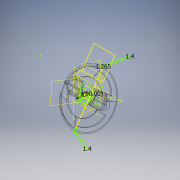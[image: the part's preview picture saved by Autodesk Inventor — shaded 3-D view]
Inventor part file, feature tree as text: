
AUTODESK INVENTOR PART (.ipt)
format: ipt  version: 2018 (Build 220112000, 112)  size: 2,839,552 bytes
history: native  units: mm
features: sketch x125, extrude x112, fillet x31, plane x11, revolve x2, hole x1, direct_edit x1, other x1
ambient origin geometry x8: Origin, YZ Plane, XZ Plane, XY Plane, X Axis, Y Axis, Z Axis, Center Point
bodies: Body1 (feature_tree)
feature tree (284):
  plane  "Work Plane5"
  sketch  "Sketch28"  dims[d118=18.7mm d119=0.0mm d120=0.9mm d121=0.0mm]
  extrude  "Extrusion21"  Depth=0.9mm TaperAngle=0.0deg
  plane  "Work Plane4"
  extrude  "Extrusion22"  Depth=3.8mm
  extrude  "Extrusion23"  Depth=46.7mm
  plane  "Work Plane3"
  hole  "Hole6"  [1 undecoded]
  extrude  "Extrusion27"  Depth=3.8mm
  extrude  "Extrusion28"  Depth=32.03mm
  extrude  "Extrusion30"  Depth=10.0mm TaperAngle=0.0deg
  extrude  "Extrusion31"  Depth=16.3mm TaperAngle=0.0deg
  sketch  "Sketch56"  dims[d188=16.3mm d189=0.0mm d190=16.3mm d191=0.0mm]
  sketch  "Sketch57"  dims[d192=16.3mm d193=0.0mm d194=16.3mm d195=0.0mm]
  extrude  "Extrusion33"  Depth=16.3mm TaperAngle=0.0deg
  extrude  "Extrusion34"  Depth=16.3mm TaperAngle=0.0deg
  extrude  "Extrusion35"  Depth=15.9mm TaperAngle=0.0deg
  extrude  "Extrusion36"  Depth=15.9mm TaperAngle=0.0deg
  extrude  "Extrusion37"  TaperAngle=90.0deg  [1 undecoded]
  extrude  "Extrusion38"  TaperAngle=0.0deg  [1 undecoded]
  extrude  "Extrusion39"  Depth=0.2mm TaperAngle=0.0deg
  extrude  "Extrusion40"  Depth=3.17mm
  extrude  "Extrusion41"  Depth=6.1mm
  sketch  "Sketch68"  dims[d251=10.0mm d252=0.0mm d253=3.91mm d254=0.0mm]
  sketch  "Sketch69"  dims[d255=0.0mm d256=0.0mm d257=3.91mm d258=0.0mm]
  extrude  "Extrusion42"  Depth=0.8mm TaperAngle=0.0deg
  extrude  "Extrusion43"  TaperAngle=0.0deg  [1 undecoded]
  extrude  "Extrusion45"  Depth=3.91mm TaperAngle=0.0deg
  extrude  "Extrusion47"  Depth=3.91mm TaperAngle=0.0deg
  extrude  "Extrusion48"  Depth=0.6mm TaperAngle=0.0deg
  extrude  "Extrusion49"  Depth=0.199mm
  direct_edit  "Direct Edit3"
  extrude  "Extrusion51"  TaperAngle=0.0deg  [1 undecoded]
  extrude  "Extrusion52"  Depth=0.7mm TaperAngle=0.0deg
  extrude  "Extrusion53"  Depth=0.09mm TaperAngle=0.0deg
  extrude  "Extrusion54"  TaperAngle=0.0deg  [1 undecoded]
  extrude  "Extrusion55"  Depth=3.9mm TaperAngle=0.0deg
  extrude  "Extrusion60"  TaperAngle=0.0deg  [1 undecoded]
  extrude  "Extrusion61"  Depth=0.657mm
  extrude  "Extrusion62"  Depth=3.9mm TaperAngle=0.0deg
  fillet  "Fillet13"  Radius=10.0mm
  extrude  "Extrusion64"  TaperAngle=0.0deg  [1 undecoded]
  extrude  "Extrusion65"  TaperAngle=0.0deg  [1 undecoded]
  extrude  "Extrusion66"  Depth=0.253mm
  extrude  "Extrusion67"  TaperAngle=0.0deg  [1 undecoded]
  fillet  "Fillet14"  [1 undecoded]
  extrude  "Extrusion68"  Depth=15.0mm
  extrude  "Extrusion69"  Depth=22.68928mm
  extrude  "Extrusion70"  TaperAngle=90.0deg  [1 undecoded]
  fillet  "Fillet15"  [1 undecoded]
  extrude  "Extrusion71"  TaperAngle=90.0deg  [1 undecoded]
  extrude  "Extrusion72"  Depth=3.490659mm
  extrude  "Extrusion73"  Depth=2.0mm TaperAngle=0.0deg
  extrude  "Extrusion74"  TaperAngle=0.0deg  [1 undecoded]
  fillet  "Fillet16"  Radius=10.0mm
  fillet  "Fillet17"  Radius=0.22mm
  extrude  "Extrusion75"  Depth=5.0mm TaperAngle=0.0deg
  plane  "Work Plane6"
  extrude  "Extrusion78"  Depth=10.0mm TaperAngle=0.0deg
  extrude  "Extrusion79"  Depth=10.0mm TaperAngle=0.0deg
  extrude  "Extrusion80"  Depth=10.0mm TaperAngle=0.0deg
  extrude  "Extrusion81"  Depth=10.0mm TaperAngle=0.0deg
  extrude  "Extrusion82"  Depth=0.865mm
  fillet  "Fillet18"  [1 undecoded]
  fillet  "Fillet19"  Radius=5.99mm
  fillet  "Fillet20"  Radius=1.49mm
  extrude  "Extrusion83"  Depth=1.77mm
  extrude  "Extrusion84"  Depth=4.0mm TaperAngle=0.0deg
  fillet  "Fillet21"  Radius=4.0mm
  extrude  "Extrusion87"  Depth=4.0mm TaperAngle=0.0deg
  plane  "Work Plane7"
  extrude  "Extrusion88"  TaperAngle=0.0deg  [1 undecoded]
  extrude  "Extrusion89"  Depth=7.0mm TaperAngle=0.0deg
  extrude  "Extrusion90"  Depth=10.0mm TaperAngle=0.0deg
  extrude  "Extrusion91"  Depth=7.0mm TaperAngle=0.0deg
  fillet  "Fillet27"  Radius=7.0mm
  extrude  "Extrusion93"  Depth=7.0mm TaperAngle=0.0deg
  extrude  "Extrusion94"  Depth=1.7mm TaperAngle=0.0deg
  fillet  "Fillet29"  [1 undecoded]
  extrude  "Extrusion95"  Depth=10.0mm TaperAngle=0.0deg
  extrude  "Extrusion97"  Depth=10.0mm TaperAngle=0.0deg
  extrude  "Extrusion98"  Depth=1.0mm TaperAngle=0.0deg
  extrude  "Extrusion99"  Depth=15.687mm
  extrude  "Extrusion100"  Depth=9.4mm
  extrude  "Extrusion101"  TaperAngle=90.0deg  [1 undecoded]
  extrude  "Extrusion102"  Depth=10.0mm TaperAngle=0.0deg
  extrude  "Extrusion104"  Depth=50.0mm TaperAngle=0.0deg
  fillet  "Fillet30"  Radius=50.0mm
  extrude  "Extrusion106"  Depth=50.0mm TaperAngle=0.0deg
  fillet  "Fillet33"  Radius=32.0mm
  fillet  "Fillet34"  Radius=9.4mm
  fillet  "Fillet35"  [1 undecoded]
  fillet  "Fillet38"  Radius=10.0mm
  extrude  "Extrusion108"  Depth=10.0mm TaperAngle=0.0deg
  extrude  "Extrusion109"  Depth=10.0mm TaperAngle=0.0deg
  extrude  "Extrusion110"  TaperAngle=0.0deg  [1 undecoded]
  extrude  "Extrusion111"  Depth=18.0mm TaperAngle=0.0deg
  extrude  "Extrusion112"  Depth=2.0mm
  sketch  "Sketch146"  dims[d571=2.0mm d572=2.0mm]
  extrude  "Extrusion113"  Depth=2.0mm
  extrude  "Extrusion114"  Depth=2.0mm
  extrude  "Extrusion115"  Depth=2.0mm
  extrude  "Extrusion116"  Depth=2.0mm
  extrude  "Extrusion118"  Depth=2.0mm
  sketch  "Sketch154"  dims[d590=2.0mm d600=1.4mm]
  extrude  "Extrusion119"  Depth=2.0mm
  extrude  "Extrusion120"  Depth=0.7mm TaperAngle=0.0deg
  extrude  "Extrusion121"  Depth=10.0mm TaperAngle=0.0deg
  extrude  "Extrusion122"  Depth=17.0mm TaperAngle=0.0deg
  extrude  "Extrusion123"  Depth=1.4mm
  extrude  "Extrusion124"  Depth=1.265mm
  extrude  "Extrusion125"  Depth=1.0mm
  extrude  "Extrusion126"  [1 undecoded]
  extrude  "Extrusion128"  [1 undecoded]
  extrude  "Extrusion129"  [1 undecoded]
  extrude  "Extrusion130"  [1 undecoded]
  plane  "Work Plane9"
  extrude  "Extrusion133"  [1 undecoded]
  extrude  "Extrusion134"  [1 undecoded]
  plane  "Work Plane8"
  extrude  "Extrusion135"  [1 undecoded]
  plane  "Work Plane2"
  revolve  "Revolution3"  [1 undecoded]
  plane  "Work Plane10"
  extrude  "Extrusion136"  [1 undecoded]
  extrude  "Extrusion137"  [1 undecoded]
  extrude  "Extrusion138"  [1 undecoded]
  extrude  "Extrusion139"  [1 undecoded]
  sketch  "Sketch184"
  plane  "Work Plane11"
  extrude  "Extrusion140"  [1 undecoded]
  extrude  "Extrusion141"  [1 undecoded]
  extrude  "Extrusion142"  [1 undecoded]
  extrude  "Extrusion143"  [1 undecoded]
  revolve  "Revolution4"  [1 undecoded]
  extrude  "Extrusion145"  [1 undecoded]
  sketch  "Sketch192"
  extrude  "Extrusion147"  [1 undecoded]
  extrude  "Extrusion148"  [1 undecoded]
  extrude  "Extrusion149"  [1 undecoded]
  sketch  "Sketch198"
  sketch  "Sketch199"
  sketch  "Sketch200"
  extrude  "Extrusion150"  [1 undecoded]
  sketch  "Sketch201"
  sketch  "Sketch202"
  extrude  "Extrusion151"  [1 undecoded]
  extrude  "Extrusion152"  [1 undecoded]
  extrude  "Extrusion153"  [1 undecoded]
  extrude  "Extrusion154"  [1 undecoded]
  sketch  "Sketch207"
  extrude  "Extrusion155"  [1 undecoded]
  fillet  "Fillet39"  [1 undecoded]
  fillet  "Fillet40"  [1 undecoded]
  fillet  "Fillet41"  [1 undecoded]
  fillet  "Fillet42"  [1 undecoded]
  fillet  "Fillet43"  [1 undecoded]
  fillet  "Fillet44"  [1 undecoded]
  fillet  "Fillet45"  [1 undecoded]
  fillet  "Fillet46"  [1 undecoded]
  fillet  "Fillet47"  [1 undecoded]
  plane  "Work Plane12"
  extrude  "Extrusion156"  [1 undecoded]
  fillet  "Fillet48"  [1 undecoded]
  fillet  "Fillet49"  [1 undecoded]
  fillet  "Fillet50"  [1 undecoded]
  fillet  "Fillet51"  [1 undecoded]
  extrude  "Extrusion157"  [1 undecoded]
  fillet  "Fillet52"  [1 undecoded]
  extrude  "Extrusion158"  [1 undecoded]
  extrude  "Extrusion159"  [1 undecoded]
  extrude  "Extrusion161"  [1 undecoded]
  fillet  "Fillet53"  [1 undecoded]
  sketch  "Sketch213"
  sketch  "Sketch41"  dims[d122=0.7mm d123=0.0mm d128=3.8mm]
  sketch  "Sketch42"  dims[d129=3.8mm d130=46.7mm]
  sketch  "Sketch43"  dims[d134=3.8mm d135=4.369mm d136=5.824mm d137=2.0mm d138=14.3117mm d139=6.637mm d140=0.0mm d150=1.5mm d151=0.0mm]
  sketch  "Sketch50"  dims[d152=1.2mm d153=0.0mm d159=3.8mm]
  sketch  "Sketch51"  dims[d161=3.8mm d168=23.3333mm d173=32.03mm]
  sketch  "Sketch53"  dims[d174=16.015mm d175=10.0mm d176=0.0mm]
  sketch  "Sketch54"  dims[d179=0.0mm d180=0.0mm d186=16.3mm d187=0.0mm]
  sketch  "Sketch58"  dims[d196=15.9mm d197=0.0mm d198=15.9mm d199=0.0mm]
  sketch  "Sketch60"  dims[d200=15.9mm d201=0.0mm d202=15.9mm d203=0.0mm]
  sketch  "Sketch61"  dims[d209=17.0mm d210=90.0deg]
  sketch  "Sketch62"  dims[d211=6.0mm d212=0.0mm d213=0.0mm d214=0.0mm]
  sketch  "Sketch63"  dims[d225=6.0mm d226=0.0mm d230=0.2mm d231=0.0mm]
  sketch  "Sketch64"  dims[d232=3.17mm d233=3.17mm]
  sketch  "Sketch65"  dims[d235=19.4mm d236=6.1mm]
  sketch  "Sketch66"  dims[d237=0.8mm d238=0.0mm d239=0.8mm d240=0.0mm]
  sketch  "Sketch67"  dims[d246=9.0mm d247=10.0mm d248=10.0mm d249=0.0mm d250=0.0mm]
  sketch  "Sketch70"  dims[d267=0.0mm d268=0.0mm d269=0.6mm d270=0.0mm]
  sketch  "Sketch72"  dims[d271=0.0mm d272=0.0mm d273=0.199mm]
  sketch  "Sketch74"  dims[d276=0.0mm d277=0.0mm d278=0.0mm d279=0.0mm]
  sketch  "Sketch75"  dims[d280=0.7mm d281=0.0mm d282=0.7mm d283=0.0mm]
  sketch  "Sketch76"  dims[d284=3.64mm d285=0.09mm d286=0.0mm]
  sketch  "Sketch79"  dims[d287=0.09mm d288=0.0mm d289=0.0mm d290=0.0mm]
  sketch  "Sketch80"  dims[d291=0.356mm d292=3.9mm d293=0.0mm]
  sketch  "Sketch81"  dims[d294=3.9mm d295=0.0mm d296=0.0mm d297=0.0mm]
  sketch  "Sketch82"  dims[d298=3.9mm d299=0.0mm d300=0.657mm]
  sketch  "Sketch83"  dims[d301=0.886mm d302=3.9mm d303=0.0mm d313=10.0mm d314=0.0mm]
  sketch  "Sketch89"  dims[d315=10.0mm d316=0.0mm d317=0.0mm d318=0.0mm]
  sketch  "Sketch90"  dims[d319=10.0mm d320=0.0mm d321=0.0mm d322=0.0mm]
  sketch  "Sketch91"  dims[d323=0.467mm d324=0.253mm]
  sketch  "Sketch93"  dims[d325=0.195mm d326=0.0mm d327=0.0mm d328=90.0deg]
  sketch  "Sketch94"  dims[d329=90.0deg d330=15.0mm]
  sketch  "Sketch95"  dims[d332=11.0mm d333=22.68928mm]
  sketch  "Sketch96"  dims[d335=90.0deg d336=90.0deg d337=0.0mm d338=0.0mm]
  sketch  "Sketch97"  dims[d344=0.954mm d350=90.0deg]
  sketch  "Sketch98"  dims[d351=3.490659mm d352=3.490659mm]
  sketch  "Sketch99"  dims[d353=6.0mm d354=0.0mm d363=2.0mm d364=0.0mm]
  sketch  "Sketch100"  dims[d365=2.0mm d366=0.0mm d374=0.0mm d375=0.0mm d376=10.0mm d377=0.0mm d378=0.22mm]
  sketch  "Sketch101"  dims[d381=5.0mm d382=0.0mm d383=5.0mm d384=0.0mm]
  sketch  "Sketch102"  dims[d386=3.8mm d397=10.0mm d398=0.0mm]
  sketch  "Sketch103"  dims[d401=0.3mm d402=0.0mm d403=10.0mm d404=0.0mm]
  sketch  "Sketch104"  dims[d405=10.0mm d406=0.0mm d407=10.0mm d408=0.0mm]
  sketch  "Sketch106"  dims[d409=10.0mm d410=0.0mm d411=10.0mm d412=0.0mm]
  sketch  "Sketch107"  dims[d415=10.0mm d416=0.0mm d419=0.865mm d421=0.0mm d422=0.0mm d424=5.99mm d425=1.49mm]
  sketch  "Sketch108"  dims[d426=0.859mm d431=1.77mm]
  sketch  "Sketch109"  dims[d432=10.0mm d433=0.0mm d434=4.0mm d435=0.0mm d436=4.0mm d437=0.0mm]
  sketch  "Sketch110"  dims[d438=4.0mm d439=0.0mm d440=4.0mm d441=0.0mm]
  sketch  "Sketch113"  dims[d442=0.0mm d443=0.0mm d444=0.0mm d445=0.0mm]
  sketch  "Sketch114"  dims[d446=1.0mm d447=0.0mm d448=7.0mm d449=0.0mm]
  sketch  "Sketch117"  dims[d452=7.0mm d453=0.0mm d454=10.0mm d455=0.0mm]
  sketch  "Sketch118"  dims[d456=0.0mm d457=0.0mm d458=7.0mm d459=0.0mm d460=7.0mm d461=0.0mm]
  sketch  "Sketch119"  dims[d462=0.0mm d463=0.0mm d464=7.0mm d465=0.0mm]
  sketch  "Sketch120"  dims[d466=1.7mm d467=0.0mm d468=1.7mm d469=0.0mm d483=0.0mm d484=0.0mm]
  sketch  "Sketch121"  dims[d485=0.0mm d486=0.0mm d487=10.0mm d488=0.0mm]
  sketch  "Sketch123"  dims[d496=10.0mm d497=0.0mm d498=10.0mm d499=0.0mm]
  sketch  "Sketch124"  dims[d500=31.5mm d501=1.0mm d502=0.0mm]
  sketch  "Sketch126"  dims[d508=-1.0mm d509=15.687mm]
  sketch  "Sketch128"  dims[d510=90.0deg d514=9.4mm]
  sketch  "Sketch129"  dims[d516=7.0mm d519=90.0deg]
  sketch  "Sketch130"  dims[d520=2.75mm d521=0.0mm d522=10.0mm d523=0.0mm]
  sketch  "Sketch131"  dims[d524=7.0mm d525=0.0mm d527=50.0mm d528=0.0mm d529=50.0mm d530=0.0mm]
  sketch  "Sketch132"  dims[d531=50.0mm d532=0.0mm d533=50.0mm d534=0.0mm d535=32.0mm d536=0.0mm d537=9.4mm d538=7.0mm d539=90.0deg d542=10.0mm d543=0.0mm]
  sketch  "Sketch133"  dims[d546=10.0mm d547=0.0mm d548=10.0mm d549=0.0mm]
  sketch  "Sketch135"  dims[d550=31.0mm d551=0.0mm d552=10.0mm d553=0.0mm]
  sketch  "Sketch137"  dims[d554=5.5mm d555=0.0mm d556=0.0mm d557=0.0mm]
  sketch  "Sketch141"  dims[d558=5.5mm d559=0.0mm d560=18.0mm d561=0.0mm]
  sketch  "Sketch142"  dims[d562=18.0mm d563=0.0mm d564=2.0mm]
  sketch  "Sketch143"  dims[d565=2.0mm d566=2.0mm]
  sketch  "Sketch144"  dims[d567=2.0mm d568=2.0mm]
  sketch  "Sketch145"  dims[d569=2.0mm d570=2.0mm]
  sketch  "Sketch147"  dims[d573=0.0mm d574=0.0mm d575=2.0mm]
  sketch  "Sketch148"  dims[d576=2.0mm d577=2.0mm]
  sketch  "Sketch149"  dims[d578=2.0mm d579=0.7mm d580=0.0mm]
  sketch  "Sketch150"  dims[d581=2.0mm d582=10.0mm d583=0.0mm]
  sketch  "Sketch153"  dims[d584=2.15mm d585=0.0mm d588=17.0mm d589=0.0mm]
  sketch  "Sketch156"  dims[d601=1.4mm d603=1.265mm]
  sketch  "Sketch157"  dims[d21=1.0mm d22=1.0mm]
  sketch  "Sketch161"
  sketch  "Sketch162"
  sketch  "Sketch163"
  sketch  "Sketch164"
  sketch  "Sketch165"
  sketch  "Sketch166"
  sketch  "Sketch169"
  sketch  "Sketch170"
  sketch  "Sketch171"
  sketch  "Sketch174"
  sketch  "Sketch175"
  sketch  "Sketch176"
  sketch  "Sketch179"
  sketch  "Sketch180"
  sketch  "Sketch181"
  sketch  "Sketch182"
  sketch  "Sketch183"
  sketch  "Sketch185"
  sketch  "Sketch186"
  sketch  "Sketch187"
  sketch  "Sketch188"
  sketch  "Sketch190"
  sketch  "Sketch193"
  sketch  "Sketch194"
  sketch  "Sketch195"
  sketch  "Sketch204"
  sketch  "Sketch205"
  sketch  "Sketch206"
  sketch  "Sketch208"
  sketch  "Sketch209"
  sketch  "Sketch210"
  sketch  "Sketch211"
  sketch  "Sketch212"
  other  "Scale3"
note: 68 required parameter values undecoded (feature->parameter linkage not recoverable at this tier; creation-order binding heuristic only, values carry confidence <= 0.55)
